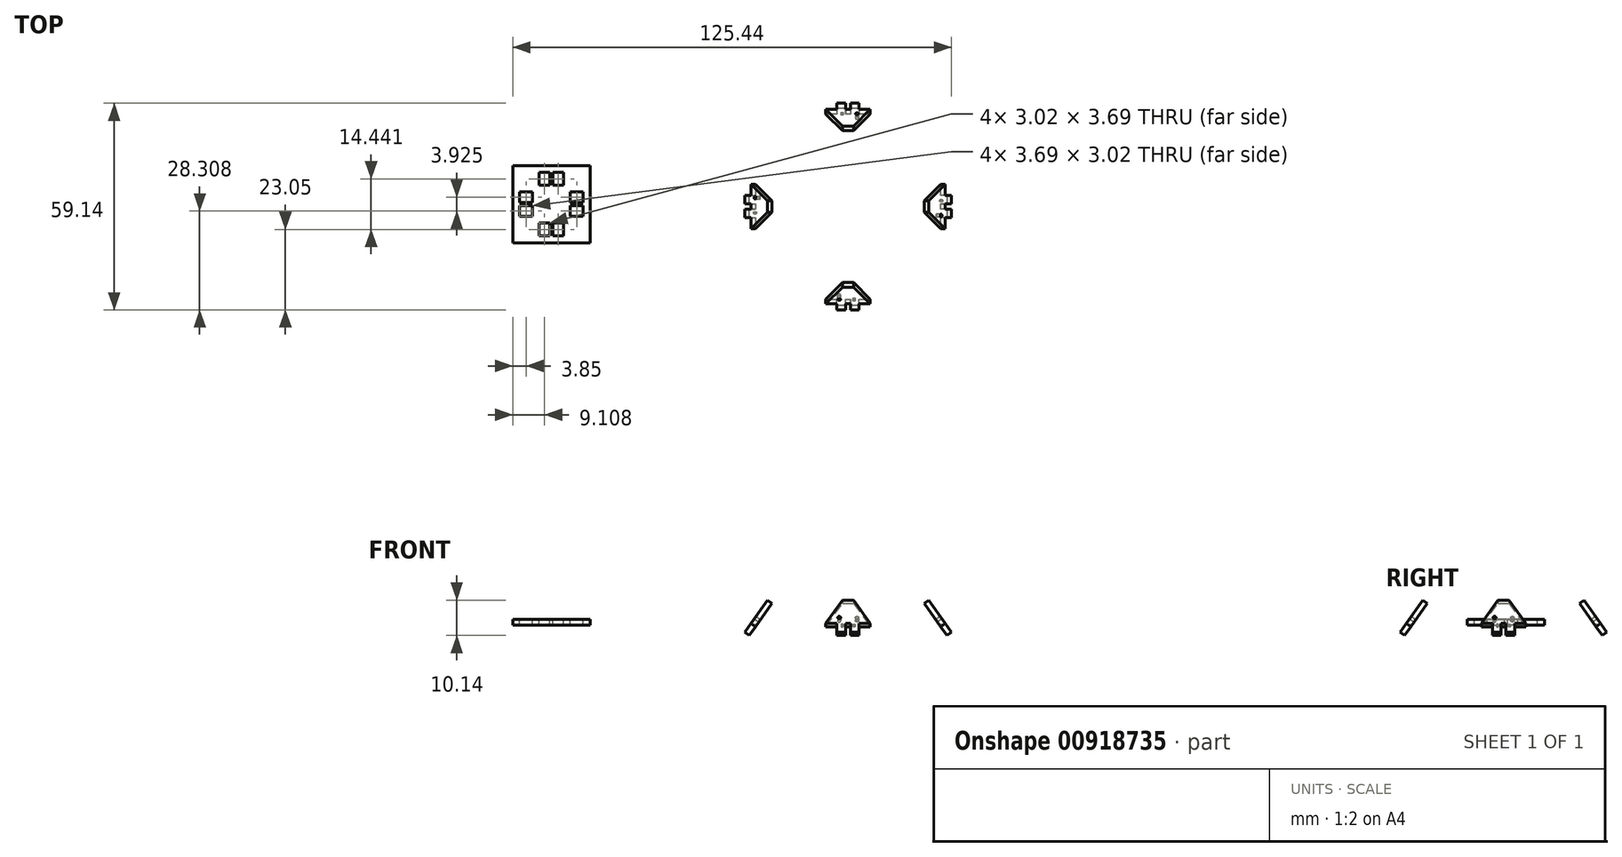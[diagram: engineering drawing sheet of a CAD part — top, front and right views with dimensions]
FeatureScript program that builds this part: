
annotation { "Feature Type Name" : "Feature", "Feature Type Description" : "" }
export const myFeature = defineFeature(function(context is Context, id is Id, definition is map)
    precondition{}
    {
        {
            var Q0;
            Q0=qCreatedBy(makeId("Top.planeOp"),FACE);
            var sketch = newSketch(context, id + "F0", { "sketchPlane" : qUnion([Q0])});
            skLineSegment(sketch, "E0", {"start": v(0, 0) * mm, "end": v(0, 27.35) * mm});
            skLineSegment(sketch, "E1", {"start": v(0, 0) * mm, "end": v(10, 0) * mm});
            skLineSegment(sketch, "E2", {"start": v(10, 0) * mm, "end": v(10, -10) * mm});
            skLineSegment(sketch, "E3", {"start": v(10, -10) * mm, "end": v(0, 0) * mm});
            skLineSegment(sketch, "E4", {"start": v(-60.25, -8.37) * mm, "end": v(-60.25, -4.67) * mm});
            skLineSegment(sketch, "E5", {"start": v(-63.27, -8.37) * mm, "end": v(-63.27, -4.97) * mm});
            skLineSegment(sketch, "E6", {"start": v(-63.27, -4.97) * mm, "end": v(-63.27, -4.67) * mm});
            skLineSegment(sketch, "E7", {"start": v(-63.27, -4.67) * mm, "end": v(-60.25, -4.67) * mm});
            skLineSegment(sketch, "E8", {"start": v(-63.27, -8.37) * mm, "end": v(-60.25, -8.37) * mm});
            skLineSegment(sketch, "E9", {"start": v(-63.27, -8.37) * mm, "end": v(-63.27, -8.07) * mm});
            skLineSegment(sketch, "E10", {"start": v(-59.35, -8.37) * mm, "end": v(-59.35, -4.67) * mm});
            skLineSegment(sketch, "E11", {"start": v(-56.33, -8.37) * mm, "end": v(-56.33, -4.97) * mm});
            skLineSegment(sketch, "E12", {"start": v(-56.33, -4.97) * mm, "end": v(-56.33, -4.67) * mm});
            skLineSegment(sketch, "E13", {"start": v(-56.33, -4.67) * mm, "end": v(-59.35, -4.67) * mm});
            skLineSegment(sketch, "E14", {"start": v(-56.33, -8.37) * mm, "end": v(-59.35, -8.37) * mm});
            skLineSegment(sketch, "E15", {"start": v(-56.33, -8.37) * mm, "end": v(-56.33, -8.07) * mm});
            skLineSegment(sketch, "E16", {"start": v(-50.73, 1.15) * mm, "end": v(-54.43, 1.15) * mm});
            skLineSegment(sketch, "E17", {"start": v(-50.73, 4.17) * mm, "end": v(-54.13, 4.17) * mm});
            skLineSegment(sketch, "E18", {"start": v(-54.13, 4.17) * mm, "end": v(-54.43, 4.17) * mm});
            skLineSegment(sketch, "E19", {"start": v(-54.43, 4.17) * mm, "end": v(-54.43, 1.15) * mm});
            skLineSegment(sketch, "E20", {"start": v(-50.73, 4.17) * mm, "end": v(-50.73, 1.15) * mm});
            skLineSegment(sketch, "E21", {"start": v(-50.73, 4.17) * mm, "end": v(-51.03, 4.17) * mm});
            skLineSegment(sketch, "E22", {"start": v(-50.73, 0.25) * mm, "end": v(-54.43, 0.25) * mm});
            skLineSegment(sketch, "E23", {"start": v(-50.73, -2.77) * mm, "end": v(-54.13, -2.77) * mm});
            skLineSegment(sketch, "E24", {"start": v(-54.13, -2.77) * mm, "end": v(-54.43, -2.77) * mm});
            skLineSegment(sketch, "E25", {"start": v(-54.43, -2.77) * mm, "end": v(-54.43, 0.25) * mm});
            skLineSegment(sketch, "E26", {"start": v(-50.73, -2.77) * mm, "end": v(-50.73, 0.25) * mm});
            skLineSegment(sketch, "E27", {"start": v(-50.73, -2.77) * mm, "end": v(-51.03, -2.77) * mm});
            skLineSegment(sketch, "E28", {"start": v(-60.25, 9.77) * mm, "end": v(-60.25, 6.07) * mm});
            skLineSegment(sketch, "E29", {"start": v(-63.27, 9.77) * mm, "end": v(-63.27, 6.37) * mm});
            skLineSegment(sketch, "E30", {"start": v(-63.27, 6.37) * mm, "end": v(-63.27, 6.07) * mm});
            skLineSegment(sketch, "E31", {"start": v(-63.27, 6.07) * mm, "end": v(-60.25, 6.07) * mm});
            skLineSegment(sketch, "E32", {"start": v(-63.27, 9.77) * mm, "end": v(-60.25, 9.77) * mm});
            skLineSegment(sketch, "E33", {"start": v(-63.27, 9.77) * mm, "end": v(-63.27, 9.47) * mm});
            skLineSegment(sketch, "E34", {"start": v(-59.35, 9.77) * mm, "end": v(-59.35, 6.07) * mm});
            skLineSegment(sketch, "E35", {"start": v(-56.33, 9.77) * mm, "end": v(-56.33, 6.37) * mm});
            skLineSegment(sketch, "E36", {"start": v(-56.33, 6.37) * mm, "end": v(-56.33, 6.07) * mm});
            skLineSegment(sketch, "E37", {"start": v(-56.33, 6.07) * mm, "end": v(-59.35, 6.07) * mm});
            skLineSegment(sketch, "E38", {"start": v(-56.33, 9.77) * mm, "end": v(-59.35, 9.77) * mm});
            skLineSegment(sketch, "E39", {"start": v(-56.33, 9.77) * mm, "end": v(-56.33, 9.47) * mm});
            skLineSegment(sketch, "E40", {"start": v(-68.87, 1.15) * mm, "end": v(-65.17, 1.15) * mm});
            skLineSegment(sketch, "E41", {"start": v(-68.87, 4.17) * mm, "end": v(-65.47, 4.17) * mm});
            skLineSegment(sketch, "E42", {"start": v(-65.47, 4.17) * mm, "end": v(-65.17, 4.17) * mm});
            skLineSegment(sketch, "E43", {"start": v(-65.17, 4.17) * mm, "end": v(-65.17, 1.15) * mm});
            skLineSegment(sketch, "E44", {"start": v(-68.87, 4.17) * mm, "end": v(-68.87, 1.15) * mm});
            skLineSegment(sketch, "E45", {"start": v(-68.87, 4.17) * mm, "end": v(-68.57, 4.17) * mm});
            skLineSegment(sketch, "E46", {"start": v(-68.87, 0.25) * mm, "end": v(-65.17, 0.25) * mm});
            skLineSegment(sketch, "E47", {"start": v(-68.87, -2.77) * mm, "end": v(-65.47, -2.77) * mm});
            skLineSegment(sketch, "E48", {"start": v(-65.47, -2.77) * mm, "end": v(-65.17, -2.77) * mm});
            skLineSegment(sketch, "E49", {"start": v(-65.17, -2.77) * mm, "end": v(-65.17, 0.25) * mm});
            skLineSegment(sketch, "E50", {"start": v(-68.87, -2.77) * mm, "end": v(-68.87, 0.25) * mm});
            skLineSegment(sketch, "E51", {"start": v(-68.87, -2.77) * mm, "end": v(-68.57, -2.77) * mm});
            skLineSegment(sketch, "E52", {"start": v(-48.73, 0.7) * mm, "end": v(-48.73, -10.37) * mm});
            skLineSegment(sketch, "E53", {"start": v(-48.73, -10.37) * mm, "end": v(-59.8, -10.37) * mm});
            skLineSegment(sketch, "E54", {"start": v(-70.87, 0.7) * mm, "end": v(-70.87, -10.37) * mm});
            skLineSegment(sketch, "E55", {"start": v(-70.87, -10.37) * mm, "end": v(-59.8, -10.37) * mm});
            skLineSegment(sketch, "E56", {"start": v(-48.73, 0.7) * mm, "end": v(-48.73, 11.77) * mm});
            skLineSegment(sketch, "E57", {"start": v(-48.73, 11.77) * mm, "end": v(-59.8, 11.77) * mm});
            skLineSegment(sketch, "E58", {"start": v(-70.87, 0.7) * mm, "end": v(-70.87, 11.77) * mm});
            skLineSegment(sketch, "E59", {"start": v(-70.87, 11.77) * mm, "end": v(-59.8, 11.77) * mm});
            skSolve(sketch);
        }
        {
            var Q0;
            Q0=sQuery(id+"F0.wireOp",EDGE,"E0");
            cPlane(context, id + "F1", {"entities" : qUnion([Q0]), "cplaneType" : CPlaneType.LINE_ANGLE, "offset" : 25 * mm, "angle" : 54.74 * degree, "oppositeDirection" : true, "width" : 150 * mm, "height" : 150 * mm});
        }
        {
            var Q0;
            Q0=qCreatedBy(id+"F1.planeOp",FACE);
            var sketch = newSketch(context, id + "F2", { "sketchPlane" : qUnion([Q0])});
            skLineSegment(sketch, "E60", {"start": v(6.35, -2.55) * mm, "end": v(1.62, 5.64) * mm});
            skLineSegment(sketch, "E61", {"start": v(-1.62, 5.64) * mm, "end": v(-6.35, -2.55) * mm});
            skLineSegment(sketch, "E62", {"start": v(3.18, -5.64) * mm, "end": v(0.75, -5.64) * mm});
            skLineSegment(sketch, "E63", {"start": v(-0.75, -5.64) * mm, "end": v(-3.18, -5.64) * mm});
            skLineSegment(sketch, "E64", {"start": v(1.62, 5.64) * mm, "end": v(-1.62, 5.64) * mm});
            skLineSegment(sketch, "E65", {"start": v(-3.18, -5.64) * mm, "end": v(-3.18, -2.55) * mm});
            skLineSegment(sketch, "E66", {"start": v(3.18, -5.64) * mm, "end": v(3.18, -2.55) * mm});
            skLineSegment(sketch, "E67", {"start": v(-6.35, -2.55) * mm, "end": v(-3.18, -2.55) * mm});
            skLineSegment(sketch, "E68", {"start": v(3.18, -2.55) * mm, "end": v(6.35, -2.55) * mm});
            skLineSegment(sketch, "E69", {"start": v(-0.75, -5.64) * mm, "end": v(-0.75, -2.55) * mm});
            skCircle(sketch, "E70", {"center": v(-2.55, -0.48) * mm, "radius": 0.42 * mm});
            skLineSegment(sketch, "E71", {"start": v(-0.75, -2.55) * mm, "end": v(0.75, -2.55) * mm});
            skLineSegment(sketch, "E72", {"start": v(0.75, -2.55) * mm, "end": v(0.75, -5.64) * mm});
            skLineSegment(sketch, "E73", {"start": v(1.96, -2.55) * mm, "end": v(1.46, -2.55) * mm});
            skLineSegment(sketch, "E74", {"start": v(1.46, -2.55) * mm, "end": v(1.46, -2.05) * mm});
            skLineSegment(sketch, "E75", {"start": v(1.46, -2.05) * mm, "end": v(1.96, -2.05) * mm});
            skLineSegment(sketch, "E76", {"start": v(1.96, -2.05) * mm, "end": v(1.96, -2.55) * mm});
            skSolve(sketch);
        }
        {
            var Q0;
            Q0 = qSketchRegion(id + "F2", true);
            var Q1;
            Q1=makeQuery(id+"F2.imprint","IMPRINT",FACE,{"disambiguationData":[TD([[makeQuery(id+"F2.imprint","IMPRINT",EDGE,{"derivedFrom":sQuery(id+"F2.wireOp",EDGE,"E73")}),-1.0]])]});
            extrude(context, id + "F3", {"entities" : qUnion([Q0, Q1]), "depth" : 1.6 * mm, "offsetDistance" : 25 * mm});
        }
        {
            var Q0;
            Q0=makeQuery(id+"F2.imprint","IMPRINT",FACE,{"disambiguationData":[TD([[makeQuery(id+"F2.imprint","IMPRINT",EDGE,{"derivedFrom":sQuery(id+"F2.wireOp",EDGE,"E73")}),-1.0]])]});
            extrude(context, id + "F4", {"entities" : qUnion([Q0]), "operationType" : NewBodyOperationType.REMOVE, "depth" : .6 * mm, "offsetDistance" : 25 * mm});
        }
        {
            var Q0;
            Q0=qCreatedBy(makeId("Right.planeOp"),FACE);
            cPlane(context, id + "F5", {"entities" : qUnion([Q0]), "cplaneType" : CPlaneType.OFFSET, "offset" : 25 * mm, "width" : 150 * mm, "height" : 150 * mm});
        }
        {
            var Q0;
            Q0=qCreatedBy(id+"F5.planeOp",FACE);
            var sketch = newSketch(context, id + "F6", { "sketchPlane" : qUnion([Q0])});
            skLineSegment(sketch, "E77", {"start": v(0, 0) * mm, "end": v(0, 26.14) * mm});
            skSolve(sketch);
        }
        {
            var Q0;
            Q0=makeQuery(id+"F3.opExtrude","SWEPT_BODY",BODY,{"disambiguationData":[OSD([sQuery(id+"F2.wireOp",EDGE,"E60"),sQuery(id+"F2.wireOp",EDGE,"E61"),sQuery(id+"F2.wireOp",EDGE,"E62"),sQuery(id+"F2.wireOp",EDGE,"E63"),sQuery(id+"F2.wireOp",EDGE,"E64"),sQuery(id+"F2.wireOp",EDGE,"E65"),sQuery(id+"F2.wireOp",EDGE,"E66"),sQuery(id+"F2.wireOp",EDGE,"E67"),sQuery(id+"F2.wireOp",EDGE,"E68"),sQuery(id+"F2.wireOp",EDGE,"E69"),sQuery(id+"F2.wireOp",EDGE,"E70"),sQuery(id+"F2.wireOp",EDGE,"E71"),sQuery(id+"F2.wireOp",EDGE,"E72")])]});
            var Q1;
            Q1=sQuery(id+"F6.wireOp",EDGE,"E77");
            circularPattern(context, id + "F7", {"entities" : qUnion([Q0]), "axis" : qUnion([Q1]), "angle" : 360 * degree, "instanceCount" : 4, "equalSpace" : true});
        }
        {
            var Q0;
            Q0=makeQuery(id+"F0.imprint","IMPRINT",FACE,{"disambiguationData":[TD([[makeQuery(id+"F0.imprint","IMPRINT",EDGE,{"derivedFrom":sQuery(id+"F0.wireOp",EDGE,"E4")}),-1.0]])]});
            extrude(context, id + "F8", {"entities" : qUnion([Q0]), "oppositeDirection" : true, "depth" : 1.6 * mm, "offsetDistance" : 25 * mm});
        }
    });
